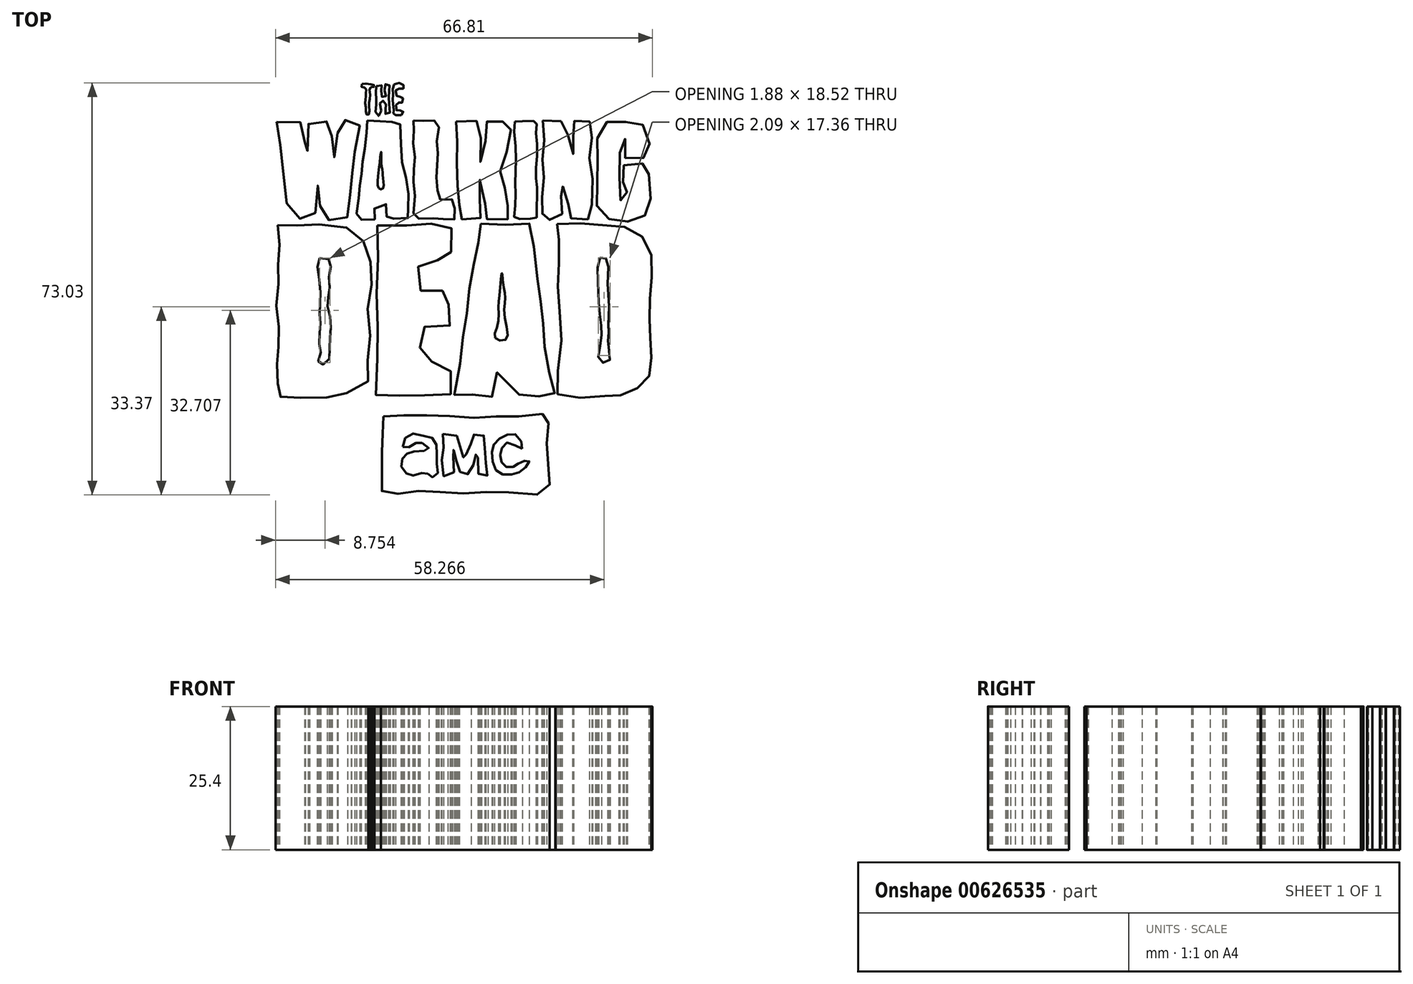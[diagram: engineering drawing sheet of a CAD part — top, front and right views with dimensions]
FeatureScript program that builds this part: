
annotation { "Feature Type Name" : "Feature", "Feature Type Description" : "" }
export const myFeature = defineFeature(function(context is Context, id is Id, definition is map)
    precondition{}
    {
        {
            var Q0;
            Q0=qCreatedBy(makeId("Top.planeOp"),FACE);
            var sketch = newSketch(context, id + "F0", { "sketchPlane" : qUnion([Q0])});
            skFitSpline(sketch, "E0", {"points": [v(-23.33, 32.74) * mm, v(-21.2, 32.74) * mm, v(-19.15, 32.65) * mm, v(-18.9, 31.71) * mm, v(-18.55, 30.1) * mm, v(-18.3, 28.3) * mm, v(-18.38, 26.77) * mm, v(-17.61, 28.39) * mm, v(-17.7, 31.29) * mm, v(-17.44, 32.82) * mm, v(-15.74, 32.82) * mm, v(-14.46, 32.82) * mm, v(-13.69, 32.82) * mm, v(-13.52, 31.12) * mm, v(-13.52, 29.33) * mm, v(-13.26, 27.7) * mm, v(-13.1, 26.43) * mm, v(-12.58, 29.07) * mm, v(-12.58, 31.54) * mm, v(-12.41, 33.08) * mm, v(-11.13, 33.08) * mm, v(-9.77, 32.82) * mm, v(-8.74, 32.82) * mm, v(-8.91, 30.78) * mm, v(-9.51, 28.13) * mm, v(-9.51, 26.17) * mm, v(-9.77, 24.55) * mm, v(-10.1, 22.6) * mm, v(-10.1, 20.8) * mm, v(-10.53, 19.18) * mm, v(-10.8, 17.3) * mm, v(-11.05, 15.51) * mm, v(-12.58, 15.34) * mm, v(-13.95, 15.34) * mm, v(-14.8, 15.34) * mm, v(-15.31, 15.17) * mm, v(-15.74, 20.71) * mm, v(-16, 22.16) * mm, v(-16.16, 19.78) * mm, v(-16.5, 17.13) * mm, v(-16.67, 15.85) * mm, v(-17.7, 15.51) * mm, v(-19.66, 15.6) * mm, v(-20.94, 15.6) * mm, v(-21.62, 19.6) * mm, v(-21.96, 22.33) * mm, v(-22.39, 25.57) * mm, v(-22.73, 28.73) * mm, v(-22.98, 31.03) * mm, v(-23.33, 32.74) * mm]});
            skFitSpline(sketch, "E1", {"points": [v(-7.3, 33) * mm, v(-4.82, 32.82) * mm, v(-2.86, 32.74) * mm, v(-1.67, 32.74) * mm, v(-1.33, 27.88) * mm, v(-0.73, 24.04) * mm, v(0, 20.2) * mm, v(0, 17.22) * mm, v(0, 15.77) * mm, v(-2.6, 15.6) * mm, v(-3.88, 15.6) * mm, v(-3.63, 17.9) * mm, v(-5.93, 17.73) * mm, v(-5.76, 15.68) * mm, v(-7.9, 15.43) * mm, v(-9.09, 15.68) * mm, v(-8.91, 18.33) * mm, v(-8.66, 20.97) * mm, v(-8.4, 22.93) * mm, v(-8.15, 25.23) * mm, v(-7.9, 27.28) * mm, v(-7.38, 30.86) * mm, v(-7.3, 33) * mm]});
            skFitSpline(sketch, "E2", {"points": [v(0.9, 33) * mm, v(2.17, 33) * mm, v(3.96, 32.9) * mm, v(5.24, 32.82) * mm, v(5.24, 30.6) * mm, v(5.07, 28.22) * mm, v(5.33, 26.26) * mm, v(4.9, 23.87) * mm, v(5.16, 21.74) * mm, v(5.24, 19.44) * mm, v(6.18, 18.92) * mm, v(7.97, 18.92) * mm, v(8.23, 17.39) * mm, v(8.23, 15.51) * mm, v(6.43, 15.51) * mm, v(5.24, 15.6) * mm, v(2.43, 15.68) * mm, v(1.06, 15.68) * mm, v(1.15, 19.1) * mm, v(0.9, 22) * mm, v(0.98, 24.47) * mm, v(1.15, 26.68) * mm, v(0.8, 29.41) * mm, v(0.98, 31.63) * mm, v(0.9, 33) * mm]});
            skFitSpline(sketch, "E3", {"points": [v(8.48, 32.82) * mm, v(8.65, 30.44) * mm, v(8.57, 27.88) * mm, v(8.65, 24.8) * mm, v(8.74, 21.74) * mm, v(8.9, 18.92) * mm, v(9, 17.39) * mm, v(9, 15.68) * mm, v(11.12, 15.6) * mm, v(12.74, 15.68) * mm, v(12.57, 17.39) * mm, v(12.83, 20.54) * mm, v(12.66, 22.5) * mm, v(13.43, 18.92) * mm, v(13.77, 17.39) * mm, v(13.85, 15.6) * mm, v(16.07, 15.68) * mm, v(18.12, 15.6) * mm, v(17.78, 17.39) * mm, v(17.35, 18.92) * mm, v(17.1, 21.31) * mm, v(16.58, 23.1) * mm, v(16.24, 24.55) * mm, v(17.35, 27.2) * mm, v(17.86, 29.75) * mm, v(18.2, 32.82) * mm, v(16.92, 32.82) * mm, v(15.56, 32.82) * mm, v(13.94, 32.82) * mm, v(13.77, 30.6) * mm, v(13.34, 27.88) * mm, v(12.74, 25.66) * mm, v(12.74, 29.07) * mm, v(12.74, 32.82) * mm, v(10.95, 32.82) * mm, v(8.48, 32.82) * mm]});
            skFitSpline(sketch, "E4", {"points": [v(-5.25, 20.97) * mm, v(-4.48, 20.97) * mm, v(-4.48, 22.76) * mm, v(-4.57, 23.95) * mm, v(-4.82, 25.83) * mm, v(-4.82, 27.45) * mm, v(-5.16, 24.98) * mm, v(-5.33, 23.44) * mm, v(-5.25, 20.97) * mm]});
            skFitSpline(sketch, "E5", {"points": [v(18.88, 32.82) * mm, v(18.97, 29.07) * mm, v(19.05, 24.8) * mm, v(18.97, 21.4) * mm, v(18.97, 18.33) * mm, v(18.88, 15.6) * mm, v(20.93, 15.68) * mm, v(22.64, 15.6) * mm, v(22.72, 18.24) * mm, v(22.9, 20.46) * mm, v(22.64, 22.6) * mm, v(22.72, 25.57) * mm, v(22.8, 29.16) * mm, v(22.64, 31.88) * mm, v(22.72, 32.82) * mm, v(20.5, 32.82) * mm, v(18.88, 32.82) * mm]});
            skFitSpline(sketch, "E6", {"points": [v(23.83, 33) * mm, v(24, 30.44) * mm, v(23.92, 27.88) * mm, v(23.74, 25.15) * mm, v(24, 23.02) * mm, v(23.74, 20.29) * mm, v(23.74, 18.07) * mm, v(23.74, 16.28) * mm, v(23.74, 15.43) * mm, v(25.45, 15.43) * mm, v(27.07, 15.77) * mm, v(27.16, 17.64) * mm, v(27.07, 19.78) * mm, v(26.99, 21.65) * mm, v(27.67, 20.71) * mm, v(28.26, 18.41) * mm, v(28.7, 16.7) * mm, v(28.95, 15.6) * mm, v(30.9, 15.6) * mm, v(32.44, 15.6) * mm, v(32.53, 18.58) * mm, v(32.61, 23.02) * mm, v(32.1, 26) * mm, v(32.53, 29.07) * mm, v(32.44, 31.37) * mm, v(32.1, 32.82) * mm, v(30.23, 32.82) * mm, v(29.29, 32.82) * mm, v(29.2, 30.52) * mm, v(29.2, 29.07) * mm, v(29.2, 27.02) * mm, v(28.35, 29.75) * mm, v(27.75, 32.82) * mm, v(26.13, 32.82) * mm, v(23.83, 33) * mm]});
            skFitSpline(sketch, "E7", {"points": [v(38.41, 26.34) * mm, v(40.03, 26.34) * mm, v(41.9, 26.34) * mm, v(42.85, 26.51) * mm, v(42.59, 29.75) * mm, v(42.16, 31.37) * mm, v(40.8, 32.82) * mm, v(39.26, 32.82) * mm, v(37.22, 32.82) * mm, v(35.51, 32.82) * mm, v(34.15, 31.88) * mm, v(33.47, 29.75) * mm, v(33.2, 27.88) * mm, v(33.72, 24.98) * mm, v(33.47, 22) * mm, v(33.47, 18.92) * mm, v(33.47, 17.39) * mm, v(34.74, 15.85) * mm, v(36.54, 15.34) * mm, v(38.16, 15.09) * mm, v(40.46, 15.34) * mm, v(41.74, 16.02) * mm, v(42.68, 17.05) * mm, v(42.93, 18.92) * mm, v(42.68, 22.42) * mm, v(42.68, 24.3) * mm, v(42.42, 25.49) * mm, v(40.2, 25.15) * mm, v(38.41, 25.32) * mm, v(38.07, 24.21) * mm, v(38.07, 22.6) * mm, v(38.16, 21.9) * mm, v(38.58, 21.82) * mm, v(38.75, 20.8) * mm, v(38.75, 19.78) * mm, v(38.75, 19) * mm, v(37.64, 18.84) * mm, v(37.39, 21.31) * mm, v(37.39, 24.38) * mm, v(37.47, 27.54) * mm, v(37.47, 29.07) * mm, v(38.41, 29.75) * mm, v(38.58, 29.07) * mm, v(38.41, 26.34) * mm]});
            skFitSpline(sketch, "E8", {"points": [v(-23.16, 14.49) * mm, v(-22.9, 11.85) * mm, v(-23.07, 8.86) * mm, v(-22.98, 6.13) * mm, v(-23.07, 3.49) * mm, v(-23.41, 0) * mm, v(-22.98, -3.16) * mm, v(-22.9, -6.15) * mm, v(-23.24, -8.62) * mm, v(-23.24, -10.58) * mm, v(-23.07, -13.3) * mm, v(-23.5, -15.44) * mm, v(-21.8, -16.12) * mm, v(-18.72, -16.12) * mm, v(-13.95, -16.04) * mm, v(-11.3, -15.44) * mm, v(-7.3, -13.48) * mm, v(-7.3, -10.58) * mm, v(-6.7, -6.66) * mm, v(-7.3, -1.63) * mm, v(-6.61, 2.98) * mm, v(-6.53, 6.47) * mm, v(-7.3, 10.31) * mm, v(-9, 12.78) * mm, v(-12.58, 14.49) * mm, v(-18.04, 14.4) * mm, v(-20.51, 14.49) * mm, v(-23.16, 14.49) * mm]});
            skFitSpline(sketch, "E9", {"points": [v(-15.74, 8.6) * mm, v(-16, 5.96) * mm, v(-15.57, 1.87) * mm, v(-15.74, -1.12) * mm, v(-15.57, -3.42) * mm, v(-15.82, -6.23) * mm, v(-15.57, -8.45) * mm, v(-15.9, -9.98) * mm, v(-14.46, -9.98) * mm, v(-13.95, -7.6) * mm, v(-13.86, -4.95) * mm, v(-13.86, -1.88) * mm, v(-14.37, 0.76) * mm, v(-13.95, 2.98) * mm, v(-14.03, 5.96) * mm, v(-13.78, 8.1) * mm, v(-15.74, 8.6) * mm]});
            skFitSpline(sketch, "E10", {"points": [v(-5.5, 14.4) * mm, v(-2.69, 14.57) * mm, v(0, 14.4) * mm, v(1.91, 14.75) * mm, v(3.88, 14.75) * mm, v(6.18, 14.49) * mm, v(7.63, 14.32) * mm, v(7.46, 12.95) * mm, v(7.46, 11.33) * mm, v(7.63, 9.37) * mm, v(7.8, 8.52) * mm, v(5.84, 8.26) * mm, v(4.22, 8.26) * mm, v(2.26, 8.1) * mm, v(1.74, 6.73) * mm, v(1.91, 5.2) * mm, v(2.17, 2.9) * mm, v(2.94, 2.72) * mm, v(5.07, 2.72) * mm, v(6.43, 2.9) * mm, v(7.46, 2.9) * mm, v(7.2, 0.85) * mm, v(7.03, -1.2) * mm, v(7.29, -2.57) * mm, v(7.29, -3.42) * mm, v(4.9, -3.42) * mm, v(2.85, -3.59) * mm, v(2.26, -3.59) * mm, v(2, -6.4) * mm, v(2, -7.85) * mm, v(1.91, -9.22) * mm, v(4.9, -9.64) * mm, v(7.37, -9.64) * mm, v(7.46, -12.12) * mm, v(7.54, -13.82) * mm, v(7.63, -15.36) * mm, v(5.5, -15.7) * mm, v(3.36, -15.7) * mm, v(1.74, -15.78) * mm, v(0, -15.78) * mm, v(-3.2, -15.7) * mm, v(-4.9, -15.61) * mm, v(-5.76, -15.61) * mm, v(-5.76, -11.52) * mm, v(-5.42, -7.34) * mm, v(-5.5, -4.19) * mm, v(-5.25, 0) * mm, v(-5.76, 3.06) * mm, v(-5.5, 7.58) * mm, v(-5.33, 10.74) * mm, v(-5.5, 14.4) * mm]});
            skFitSpline(sketch, "E11", {"points": [v(15.39, -5.55) * mm, v(17.35, -5.8) * mm, v(17, -1.46) * mm, v(17.18, 1.61) * mm, v(16.84, 3.74) * mm, v(16.58, 6.05) * mm, v(16.24, 2.98) * mm, v(15.98, 0) * mm, v(15.81, -3.33) * mm, v(15.39, -5.55) * mm]});
            skFitSpline(sketch, "E12", {"points": [v(12.83, 14.75) * mm, v(15.81, 14.66) * mm, v(20.33, 14.57) * mm, v(21.78, 14.57) * mm, v(22.3, 10.23) * mm, v(22.98, 4.43) * mm, v(23.4, 1.53) * mm, v(23.74, -1.2) * mm, v(24, -4.19) * mm, v(24.17, -7.43) * mm, v(24.94, -11.43) * mm, v(25.2, -13.4) * mm, v(25.96, -16.04) * mm, v(23.49, -15.95) * mm, v(21.19, -15.7) * mm, v(18.88, -15.7) * mm, v(18.2, -15.87) * mm, v(18.12, -12.03) * mm, v(15.22, -12.12) * mm, v(14.8, -15.95) * mm, v(12.83, -15.87) * mm, v(10.27, -15.61) * mm, v(8.31, -15.87) * mm, v(9, -11) * mm, v(9.5, -6.57) * mm, v(10.19, -2.74) * mm, v(10.44, 0) * mm, v(10.95, 3.92) * mm, v(11.55, 7.07) * mm, v(11.98, 10.4) * mm, v(12.83, 12.44) * mm, v(12.83, 14.75) * mm]});
            skFitSpline(sketch, "E13", {"points": [v(33.98, 8.7) * mm, v(35.09, 8.52) * mm, v(35.43, 6.05) * mm, v(35.34, 4) * mm, v(35.6, 0) * mm, v(35.43, -2.65) * mm, v(35.51, -4.7) * mm, v(35.43, -7) * mm, v(35.6, -9.64) * mm, v(33.9, -9.64) * mm, v(34.15, -6.23) * mm, v(34.15, -3.16) * mm, v(33.72, 0.85) * mm, v(33.64, 4.34) * mm, v(33.98, 8.7) * mm]});
            skFitSpline(sketch, "E14", {"points": [v(26.39, 14.66) * mm, v(33.38, 14.49) * mm, v(37.47, 14.32) * mm, v(41.23, 12.61) * mm, v(43.19, 8.52) * mm, v(42.93, 3.23) * mm, v(42.76, -1.54) * mm, v(42.85, -5.12) * mm, v(43.1, -9.47) * mm, v(42.42, -12.8) * mm, v(39.78, -14.84) * mm, v(36.7, -15.87) * mm, v(33.47, -15.87) * mm, v(26.64, -15.7) * mm, v(26.9, -9.22) * mm, v(26.73, 0) * mm, v(26.56, 6.22) * mm, v(26.64, 12.1) * mm, v(26.39, 14.66) * mm]});
            skFitSpline(sketch, "E15", {"points": [v(-4.43, -19.46) * mm, v(-4.53, -22.37) * mm, v(-4.64, -25.7) * mm, v(-4.64, -28.72) * mm, v(-4.53, -32.92) * mm, v(-1.52, -33.14) * mm, v(2.68, -32.6) * mm, v(7.53, -33.03) * mm, v(13.02, -32.92) * mm, v(17.97, -32.92) * mm, v(24.43, -32.92) * mm, v(24.97, -30.01) * mm, v(24.65, -25.7) * mm, v(24.65, -21.61) * mm, v(24.76, -19.24) * mm, v(20.88, -19.35) * mm, v(15.71, -19.46) * mm, v(10.76, -19.67) * mm, v(4.84, -19.24) * mm, v(0, -19.35) * mm, v(-4.43, -19.46) * mm]});
            skFitSpline(sketch, "E16", {"points": [v(-0.98, -24.84) * mm, v(0, -24.95) * mm, v(1.5, -24.09) * mm, v(2.57, -24.2) * mm, v(3.65, -25.27) * mm, v(1.71, -25.6) * mm, v(0, -25.92) * mm, v(-0.98, -26.78) * mm, v(-1.2, -28.4) * mm, v(0, -29.8) * mm, v(1.39, -29.8) * mm, v(3.22, -29.37) * mm, v(3.76, -30.12) * mm, v(5.05, -29.9) * mm, v(5.05, -27.97) * mm, v(5.05, -25.49) * mm, v(4.51, -23.44) * mm, v(2.36, -22.8) * mm, v(0, -22.69) * mm, v(-0.98, -24.84) * mm]});
            skFitSpline(sketch, "E17", {"points": [v(6.13, -22.58) * mm, v(8.6, -22.9) * mm, v(9.9, -27.32) * mm, v(10.44, -25.7) * mm, v(11.08, -24.41) * mm, v(11.3, -22.8) * mm, v(12.7, -22.8) * mm, v(13.45, -22.9) * mm, v(13.56, -25.06) * mm, v(13.77, -27.97) * mm, v(13.99, -29.9) * mm, v(12.7, -30.01) * mm, v(12.37, -28.18) * mm, v(12.16, -25.7) * mm, v(11.84, -26.67) * mm, v(11.51, -27.97) * mm, v(10.97, -29.26) * mm, v(9.79, -29.9) * mm, v(9.14, -29.15) * mm, v(8.6, -27.64) * mm, v(8.17, -25.92) * mm, v(7.85, -25.17) * mm, v(8.07, -27.54) * mm, v(7.85, -29.69) * mm, v(6.24, -30.01) * mm, v(6.02, -26.67) * mm, v(6.24, -24.95) * mm, v(6.13, -22.58) * mm]});
            skFitSpline(sketch, "E18", {"points": [v(20.13, -25.17) * mm, v(17.87, -24.09) * mm, v(16.57, -25.17) * mm, v(16.36, -27) * mm, v(17.33, -28.4) * mm, v(18.84, -28.29) * mm, v(19.91, -27.54) * mm, v(21.42, -27.32) * mm, v(20.56, -28.72) * mm, v(18.62, -29.69) * mm, v(16.04, -29.47) * mm, v(14.85, -26.89) * mm, v(15.17, -24.41) * mm, v(17.22, -22.8) * mm, v(19.37, -22.9) * mm, v(20.13, -25.17) * mm]});
            skFitSpline(sketch, "E19", {"points": [v(-8.21, 39.5) * mm, v(-8.21, 38.88) * mm, v(-7.6, 38.8) * mm, v(-7.53, 37.74) * mm, v(-7.53, 37.2) * mm, v(-7.68, 36.3) * mm, v(-7.53, 35.15) * mm, v(-7.45, 34.16) * mm, v(-7.07, 34) * mm, v(-6.92, 35.23) * mm, v(-6.92, 36.3) * mm, v(-6.77, 37.43) * mm, v(-6.77, 38.88) * mm, v(-6.08, 38.96) * mm, v(-6.08, 39.26) * mm, v(-6.77, 39.41) * mm, v(-8.21, 39.5) * mm]});
            skFitSpline(sketch, "E20", {"points": [v(-5.7, 39.11) * mm, v(-5.7, 37.59) * mm, v(-5.7, 36.67) * mm, v(-5.7, 35.53) * mm, v(-5.7, 34) * mm, v(-5.02, 33.93) * mm, v(-4.94, 35.53) * mm, v(-4.94, 36.44) * mm, v(-4.03, 36.3) * mm, v(-4.03, 35.46) * mm, v(-4.1, 34.62) * mm, v(-4.1, 34.24) * mm, v(-3.34, 34.24) * mm, v(-3.5, 36.3) * mm, v(-3.42, 37.43) * mm, v(-3.42, 38.73) * mm, v(-3.42, 39.41) * mm, v(-4.18, 39.34) * mm, v(-4.1, 38.04) * mm, v(-4.03, 37.2) * mm, v(-4.71, 37.2) * mm, v(-4.79, 38.35) * mm, v(-4.79, 39.26) * mm, v(-5.7, 39.11) * mm]});
            skFitSpline(sketch, "E21", {"points": [v(-2.5, 39.41) * mm, v(-2.73, 37.59) * mm, v(-2.73, 36.14) * mm, v(-2.58, 34.54) * mm, v(-2.58, 34.09) * mm, v(-1.06, 34.09) * mm, v(-1.06, 34.77) * mm, v(-2.05, 34.77) * mm, v(-1.97, 36.14) * mm, v(-1.13, 36.14) * mm, v(-1.06, 37.13) * mm, v(-1.9, 37.2) * mm, v(-2.12, 38.58) * mm, v(-0.9, 38.66) * mm, v(-0.98, 39.41) * mm, v(-2.5, 39.41) * mm]});
            skSolve(sketch);
        }
        {
            var Q0;
            Q0 = qSketchRegion(id + "F0", true);
            extrude(context, id + "F1", {"entities" : qUnion([Q0]), "depth" : 25.4 * mm, "offsetDistance" : 25.4 * mm});
        }
    });
